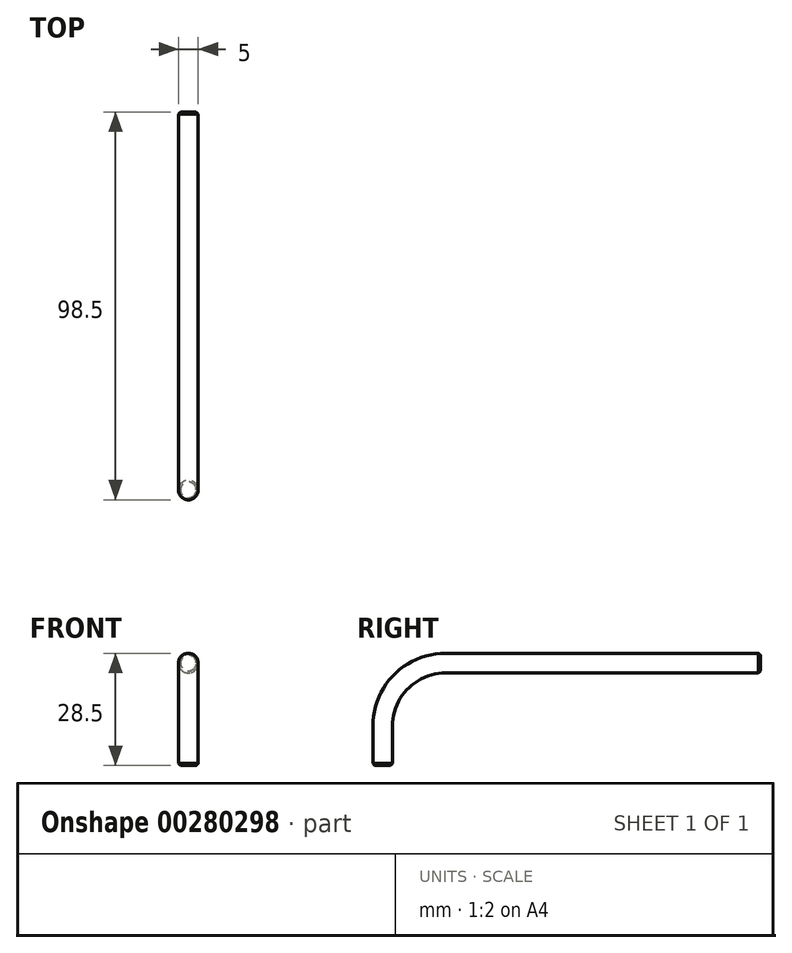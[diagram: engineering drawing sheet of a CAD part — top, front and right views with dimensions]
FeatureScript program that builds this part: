
annotation { "Feature Type Name" : "Feature", "Feature Type Description" : "" }
export const myFeature = defineFeature(function(context is Context, id is Id, definition is map)
    precondition{}
    {
        {
            var Q0;
            Q0=qCreatedBy(makeId("Top.planeOp"),FACE);
            var sketch = newSketch(context, id + "F0", { "sketchPlane" : qUnion([Q0])});
            skCircle(sketch, "E0", {"center": v(0, 0) * mm, "radius": 2.5 * mm});
            skSolve(sketch);
        }
        {
            var Q0;
            Q0=qCreatedBy(makeId("Right.planeOp"),FACE);
            var sketch = newSketch(context, id + "F1", { "sketchPlane" : qUnion([Q0])});
            skLineSegment(sketch, "E1", {"start": v(0, 0) * mm, "end": v(0, 10) * mm});
            skLineSegment(sketch, "E2", {"start": v(16, 26) * mm, "end": v(96, 26) * mm});
            skPoint(sketch, "E3.visualSharp", {"position": v(0, 26) * mm});
            skArc(sketch, "E3.filletArc", {"start": v(16, 26) * mm, "mid": v(4.69, 21.31) * mm, "end": v(0, 10) * mm});
            skSolve(sketch);
        }
        {
            var Q0;
            Q0 = qSketchRegion(id + "F0", true);
            var Q1;
            Q1 = qConstructionFilter(qBodyType(qCreatedBy(id + "F1" ,EDGE), BodyType.WIRE), ConstructionObject.NO);
            sweep(context, id + "F2", {"profiles" : qUnion([Q0]), "path" : qUnion([Q1])});
        }
        {
            var Q0;
            Q0=makeQuery(id+"F2.opSweep","CAP_EDGE",EDGE,{"disambiguationData":[OSD([sQuery(id+"F0.wireOp",EDGE,"E0"),sQuery(id+"F1.wireOp",VERTEX,"E2.end")])],"isStart":false});
            var Q1;
            Q1=makeQuery(id+"F2.opSweep","CAP_EDGE",EDGE,{"disambiguationData":[OSD([sQuery(id+"F0.wireOp",EDGE,"E0"),sQuery(id+"F1.wireOp",VERTEX,"E1.start")])],"isStart":true});
            chamfer(context, id + "F3", {"entities" : qUnion([Q0, Q1]), "chamferType" : ChamferType.OFFSET_ANGLE, "width" : .5 * mm, "oppositeDirection" : false, "angle" : 45 * degree, "tangentPropagation" : true});
        }
    });
